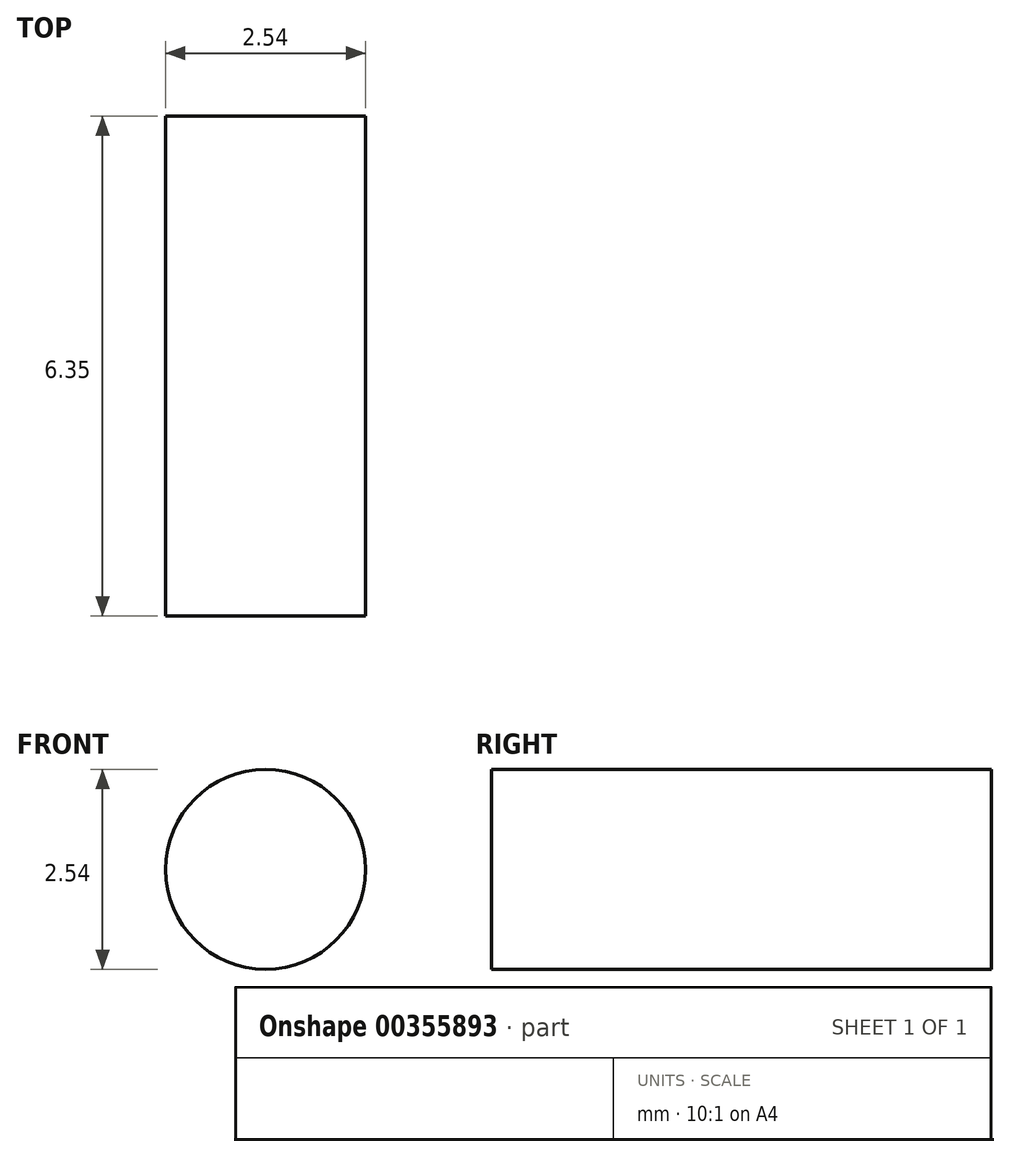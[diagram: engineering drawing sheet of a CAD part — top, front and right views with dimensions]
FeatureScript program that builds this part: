
annotation { "Feature Type Name" : "Feature", "Feature Type Description" : "" }
export const myFeature = defineFeature(function(context is Context, id is Id, definition is map)
    precondition{}
    {
        {
            var Q0;
            Q0=qCreatedBy(makeId("Front.planeOp"),FACE);
            var sketch = newSketch(context, id + "F0", { "sketchPlane" : qUnion([Q0])});
            skCircle(sketch, "E0", {"center": v(0, 0) * mm, "radius": 1.27 * mm});
            skSolve(sketch);
        }
        {
            var Q0;
            Q0=makeQuery(id+"F0.imprint","IMPRINT",FACE,{"disambiguationData":[TD([[makeQuery(id+"F0.imprint","IMPRINT",EDGE,{"derivedFrom":sQuery(id+"F0.wireOp",EDGE,"E0")}),1.0]])]});
            extrude(context, id + "F1", {"entities" : qUnion([Q0]), "depth" : 6.35 * mm});
        }
    });
